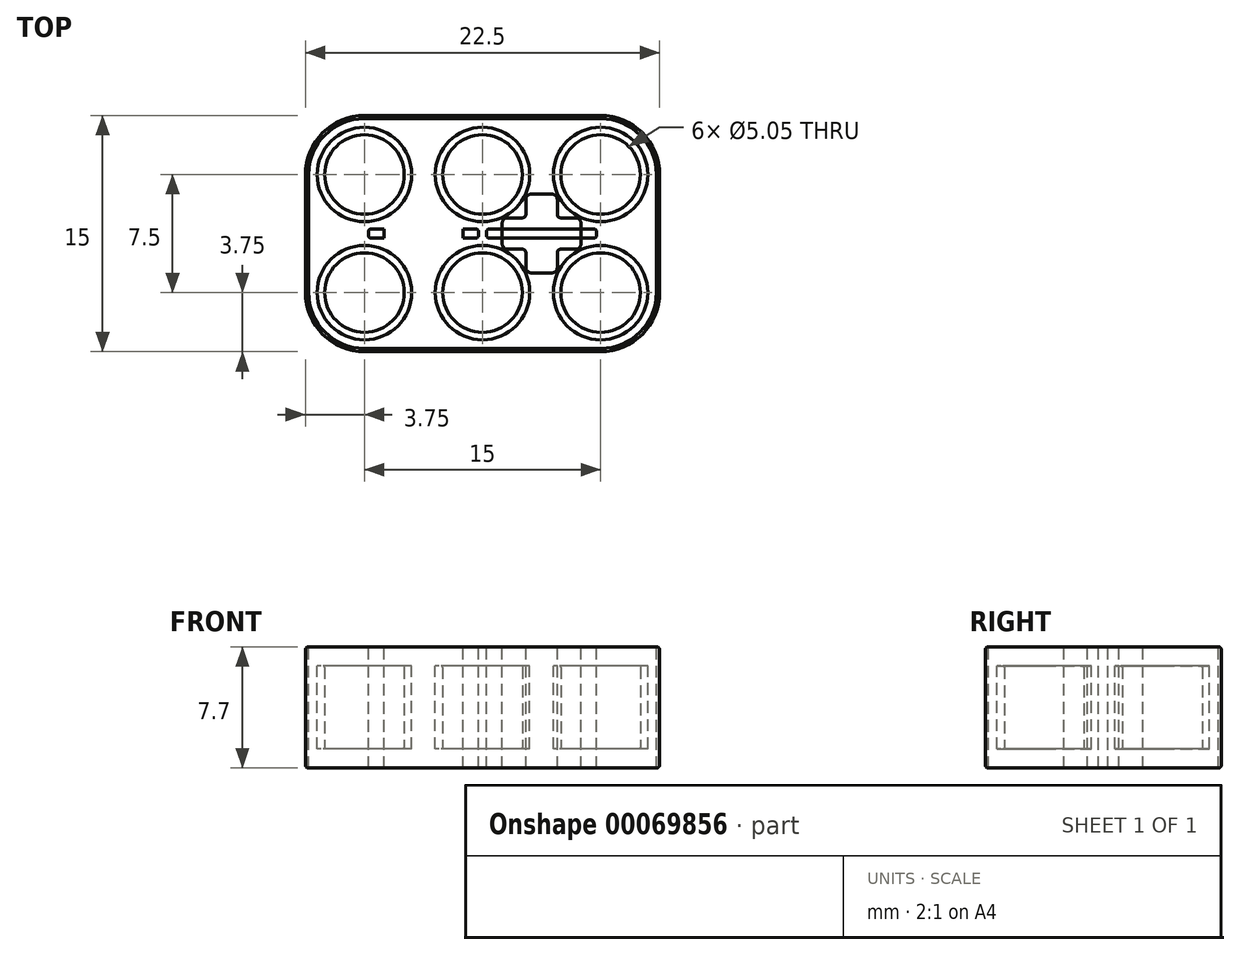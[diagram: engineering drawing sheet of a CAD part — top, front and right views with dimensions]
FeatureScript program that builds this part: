
annotation { "Feature Type Name" : "Feature", "Feature Type Description" : "" }
export const myFeature = defineFeature(function(context is Context, id is Id, definition is map)
    precondition{}
    {
        {
            var Q0;
            Q0=qCreatedBy(makeId("Top.planeOp"),FACE);
            var sketch = newSketch(context, id + "F0", { "sketchPlane" : qUnion([Q0])});
            skLineSegment(sketch, "E0.rect.bottom", {"start": v(7.5, -7.5) * mm, "end": v(-7.5, -7.5) * mm});
            skLineSegment(sketch, "E0.rect.top", {"start": v(7.5, 7.5) * mm, "end": v(-7.5, 7.5) * mm});
            skLineSegment(sketch, "E0.rect.left", {"start": v(11.25, -3.75) * mm, "end": v(11.25, 3.75) * mm});
            skLineSegment(sketch, "E0.rect.right", {"start": v(-11.25, -3.75) * mm, "end": v(-11.25, 3.75) * mm});
            skPoint(sketch, "E0.rect.middle", {"position": v(0, 0) * mm});
            skPoint(sketch, "E1.visualSharp", {"position": v(11.25, 7.5) * mm});
            skArc(sketch, "E1.filletArc", {"start": v(11.25, 3.75) * mm, "mid": v(10.15, 6.4) * mm, "end": v(7.5, 7.5) * mm});
            skPoint(sketch, "E2.visualSharp", {"position": v(-11.25, 7.5) * mm});
            skArc(sketch, "E2.filletArc", {"start": v(-7.5, 7.5) * mm, "mid": v(-10.15, 6.4) * mm, "end": v(-11.25, 3.75) * mm});
            skPoint(sketch, "E3.visualSharp", {"position": v(-11.25, -7.5) * mm});
            skArc(sketch, "E3.filletArc", {"start": v(-11.25, -3.75) * mm, "mid": v(-10.15, -6.4) * mm, "end": v(-7.5, -7.5) * mm});
            skPoint(sketch, "E4.visualSharp", {"position": v(11.25, -7.5) * mm});
            skArc(sketch, "E4.filletArc", {"start": v(7.5, -7.5) * mm, "mid": v(10.15, -6.4) * mm, "end": v(11.25, -3.75) * mm});
            skCircle(sketch, "E5", {"center": v(-7.5, 3.75) * mm, "radius": 2.52 * mm});
            skLineSegment(sketch, "E6", {"start": v(0, 0) * mm, "end": v(0, 7.5) * mm, "construction": true});
            skLineSegment(sketch, "E7", {"start": v(0, 0) * mm, "end": v(11.25, 0) * mm, "construction": true});
            skCircle(sketch, "E8.MirrorC", {"center": v(7.5, 3.75) * mm, "radius": 2.52 * mm});
            skCircle(sketch, "E9.MirrorC", {"center": v(7.5, -3.75) * mm, "radius": 2.52 * mm});
            skCircle(sketch, "E10.MirrorC", {"center": v(-7.5, -3.75) * mm, "radius": 2.52 * mm});
            skCircle(sketch, "E11", {"center": v(0, 3.75) * mm, "radius": 2.52 * mm});
            skCircle(sketch, "E12.MirrorC", {"center": v(0, -3.75) * mm, "radius": 2.52 * mm});
            skSolve(sketch);
        }
        {
            var Q0;
            Q0=qSketchRegion(id+"F0",true);
            extrude(context, id + "F1", {"entities" : qUnion([Q0]), "depth" : 3.85 * mm});
        }
        {
            var Q0;
            Q0=makeQuery(id+"F1.opExtrude","CAP_FACE",FACE,{"disambiguationData":[OSD([sQuery(id+"F0.wireOp",EDGE,"E0.rect.bottom"),sQuery(id+"F0.wireOp",EDGE,"E0.rect.top"),sQuery(id+"F0.wireOp",EDGE,"E0.rect.left"),sQuery(id+"F0.wireOp",EDGE,"E0.rect.right"),sQuery(id+"F0.wireOp",EDGE,"E1.filletArc"),sQuery(id+"F0.wireOp",EDGE,"E2.filletArc"),sQuery(id+"F0.wireOp",EDGE,"E3.filletArc"),sQuery(id+"F0.wireOp",EDGE,"E4.filletArc"),sQuery(id+"F0.wireOp",EDGE,"E5"),sQuery(id+"F0.wireOp",EDGE,"E8.MirrorC"),sQuery(id+"F0.wireOp",EDGE,"E9.MirrorC"),sQuery(id+"F0.wireOp",EDGE,"E10.MirrorC")])],"isStart":false});
            fillet(context, id + "F2", {"entities" : qUnion([Q0]), "radius" : 0.2 * mm, "tangentPropagation" : true, "allowEdgeOverflow" : false});
        }
        {
            var Q0;
            Q0=makeQuery(id+"F1.opExtrude","CAP_FACE",FACE,{"disambiguationData":[OSD([sQuery(id+"F0.wireOp",EDGE,"E0.rect.bottom"),sQuery(id+"F0.wireOp",EDGE,"E0.rect.top"),sQuery(id+"F0.wireOp",EDGE,"E0.rect.left"),sQuery(id+"F0.wireOp",EDGE,"E0.rect.right"),sQuery(id+"F0.wireOp",EDGE,"E1.filletArc"),sQuery(id+"F0.wireOp",EDGE,"E2.filletArc"),sQuery(id+"F0.wireOp",EDGE,"E3.filletArc"),sQuery(id+"F0.wireOp",EDGE,"E4.filletArc"),sQuery(id+"F0.wireOp",EDGE,"E5"),sQuery(id+"F0.wireOp",EDGE,"E8.MirrorC"),sQuery(id+"F0.wireOp",EDGE,"E9.MirrorC"),sQuery(id+"F0.wireOp",EDGE,"E10.MirrorC")])],"isStart":false});
            var sketch = newSketch(context, id + "F3", { "sketchPlane" : qUnion([Q0])});
            skCircle(sketch, "E13", {"center": v(-7.5, 3.75) * mm, "radius": 3 * mm});
            skCircle(sketch, "E14.MirrorC", {"center": v(7.5, 3.75) * mm, "radius": 3 * mm});
            skCircle(sketch, "E15.MirrorC", {"center": v(7.5, -3.75) * mm, "radius": 3 * mm});
            skCircle(sketch, "E16.MirrorC", {"center": v(-7.5, -3.75) * mm, "radius": 3 * mm});
            skCircle(sketch, "E17", {"center": v(0, 3.75) * mm, "radius": 3 * mm});
            skCircle(sketch, "E18.MirrorC", {"center": v(0, -3.75) * mm, "radius": 3 * mm});
            skSolve(sketch);
        }
        {
            var Q0;
            Q0=qSketchRegion(id+"F3",true);
            extrude(context, id + "F4", {"entities" : qUnion([Q0]), "operationType" : NewBodyOperationType.REMOVE, "oppositeDirection" : true, "depth" : 1.2 * mm});
        }
        {
            var Q0;
            Q0=makeQuery(id+"F4.boolean.opBoolean","COPY",EDGE,{"derivedFrom":makeQuery(id+"F4.opExtrude","CAP_EDGE",EDGE,{"disambiguationData":[OSD([sQuery(id+"F3.wireOp",EDGE,"E16.MirrorC")])],"isStart":true})});
            var Q1;
            Q1=makeQuery(id+"F4.boolean.opBoolean","INTERSECT",EDGE,{"derivedFrom":[makeQuery(id+"F1.opExtrude","SWEPT_FACE",FACE,{"disambiguationData":[OSD([sQuery(id+"F0.wireOp",EDGE,"E10.MirrorC")])]}),makeQuery(id+"F4.opExtrude","CAP_FACE",FACE,{"disambiguationData":[OSD([sQuery(id+"F3.wireOp",EDGE,"E16.MirrorC")])],"isStart":false})]});
            var Q2;
            Q2=makeQuery(id+"F4.boolean.opBoolean","COPY",EDGE,{"derivedFrom":makeQuery(id+"F4.opExtrude","CAP_EDGE",EDGE,{"disambiguationData":[OSD([sQuery(id+"F3.wireOp",EDGE,"E13")])],"isStart":true})});
            var Q3;
            Q3=makeQuery(id+"F4.boolean.opBoolean","INTERSECT",EDGE,{"derivedFrom":[makeQuery(id+"F1.opExtrude","SWEPT_FACE",FACE,{"disambiguationData":[OSD([sQuery(id+"F0.wireOp",EDGE,"E5")])]}),makeQuery(id+"F4.opExtrude","CAP_FACE",FACE,{"disambiguationData":[OSD([sQuery(id+"F3.wireOp",EDGE,"E13")])],"isStart":false})]});
            var Q4;
            Q4=makeQuery(id+"F4.boolean.opBoolean","COPY",EDGE,{"derivedFrom":makeQuery(id+"F4.opExtrude","CAP_EDGE",EDGE,{"disambiguationData":[OSD([sQuery(id+"F3.wireOp",EDGE,"E14.MirrorC")])],"isStart":true})});
            var Q5;
            Q5=makeQuery(id+"F4.boolean.opBoolean","INTERSECT",EDGE,{"derivedFrom":[makeQuery(id+"F1.opExtrude","SWEPT_FACE",FACE,{"disambiguationData":[OSD([sQuery(id+"F0.wireOp",EDGE,"E8.MirrorC")])]}),makeQuery(id+"F4.opExtrude","CAP_FACE",FACE,{"disambiguationData":[OSD([sQuery(id+"F3.wireOp",EDGE,"E14.MirrorC")])],"isStart":false})]});
            var Q6;
            Q6=makeQuery(id+"F4.boolean.opBoolean","INTERSECT",EDGE,{"derivedFrom":[makeQuery(id+"F1.opExtrude","SWEPT_FACE",FACE,{"disambiguationData":[OSD([sQuery(id+"F0.wireOp",EDGE,"E9.MirrorC")])]}),makeQuery(id+"F4.opExtrude","CAP_FACE",FACE,{"disambiguationData":[OSD([sQuery(id+"F3.wireOp",EDGE,"E15.MirrorC")])],"isStart":false})]});
            var Q7;
            Q7=makeQuery(id+"F4.boolean.opBoolean","COPY",EDGE,{"derivedFrom":makeQuery(id+"F4.opExtrude","CAP_EDGE",EDGE,{"disambiguationData":[OSD([sQuery(id+"F3.wireOp",EDGE,"E15.MirrorC")])],"isStart":true})});
            var Q8;
            Q8=makeQuery(id+"F4.boolean.opBoolean","COPY",EDGE,{"derivedFrom":makeQuery(id+"F4.opExtrude","CAP_EDGE",EDGE,{"disambiguationData":[OSD([sQuery(id+"F3.wireOp",EDGE,"E17")])],"isStart":true})});
            var Q9;
            Q9=makeQuery(id+"F4.boolean.opBoolean","INTERSECT",EDGE,{"derivedFrom":[makeQuery(id+"F1.opExtrude","SWEPT_FACE",FACE,{"disambiguationData":[OSD([sQuery(id+"F0.wireOp",EDGE,"E11")])]}),makeQuery(id+"F4.opExtrude","CAP_FACE",FACE,{"disambiguationData":[OSD([sQuery(id+"F3.wireOp",EDGE,"E17")])],"isStart":false})]});
            var Q10;
            Q10=makeQuery(id+"F4.boolean.opBoolean","COPY",EDGE,{"derivedFrom":makeQuery(id+"F4.opExtrude","CAP_EDGE",EDGE,{"disambiguationData":[OSD([sQuery(id+"F3.wireOp",EDGE,"E18.MirrorC")])],"isStart":true})});
            var Q11;
            Q11=makeQuery(id+"F4.boolean.opBoolean","INTERSECT",EDGE,{"derivedFrom":[makeQuery(id+"F1.opExtrude","SWEPT_FACE",FACE,{"disambiguationData":[OSD([sQuery(id+"F0.wireOp",EDGE,"E12.MirrorC")])]}),makeQuery(id+"F4.opExtrude","CAP_FACE",FACE,{"disambiguationData":[OSD([sQuery(id+"F3.wireOp",EDGE,"E18.MirrorC")])],"isStart":false})]});
            fillet(context, id + "F5", {"entities" : qUnion([Q0, Q1, Q2, Q3, Q4, Q5, Q6, Q7, Q8, Q9, Q10, Q11]), "radius" : 0.1 * mm, "tangentPropagation" : true, "allowEdgeOverflow" : false});
        }
        {
            var Q0;
            Q0=makeQuery(id+"F1.opExtrude","CAP_FACE",FACE,{"disambiguationData":[OSD([sQuery(id+"F0.wireOp",EDGE,"E0.rect.bottom"),sQuery(id+"F0.wireOp",EDGE,"E0.rect.top"),sQuery(id+"F0.wireOp",EDGE,"E0.rect.left"),sQuery(id+"F0.wireOp",EDGE,"E0.rect.right"),sQuery(id+"F0.wireOp",EDGE,"E1.filletArc"),sQuery(id+"F0.wireOp",EDGE,"E2.filletArc"),sQuery(id+"F0.wireOp",EDGE,"E3.filletArc"),sQuery(id+"F0.wireOp",EDGE,"E4.filletArc"),sQuery(id+"F0.wireOp",EDGE,"E5"),sQuery(id+"F0.wireOp",EDGE,"E8.MirrorC"),sQuery(id+"F0.wireOp",EDGE,"E9.MirrorC"),sQuery(id+"F0.wireOp",EDGE,"E10.MirrorC")])],"isStart":false});
            var sketch = newSketch(context, id + "F6", { "sketchPlane" : qUnion([Q0])});
            skPoint(sketch, "E19", {"position": v(-3.75, 0) * mm});
            skPoint(sketch, "E20.visualSharp", {"position": v(-7.25, 0.3) * mm});
            skPoint(sketch, "E21.visualSharp", {"position": v(-7.25, -0.3) * mm});
            skPoint(sketch, "E22.visualSharp", {"position": v(-4.75, -2.5) * mm});
            skPoint(sketch, "E23.visualSharp", {"position": v(-1.25, 1) * mm});
            skLineSegment(sketch, "E24.trimOffspring", {"start": v(-4.95, 1) * mm, "end": v(-5.9, 1) * mm});
            skLineSegment(sketch, "E25.trimOffspring", {"start": v(-2.75, -1.2) * mm, "end": v(-2.75, -2.15) * mm});
            skPoint(sketch, "E26.visualSharp", {"position": v(-2.75, 2.5) * mm});
            skPoint(sketch, "E27.visualSharp", {"position": v(-2.75, -2.5) * mm});
            skPoint(sketch, "E28.visualSharp", {"position": v(-6.25, 1) * mm});
            skLineSegment(sketch, "E29.rect.bottom", {"start": v(-3.1, 2.5) * mm, "end": v(-4.4, 2.5) * mm});
            skPoint(sketch, "E30.visualSharp", {"position": v(-6.25, -1) * mm});
            skPoint(sketch, "E31.visualSharp", {"position": v(-4.75, -1) * mm});
            skPoint(sketch, "E32.visualSharp", {"position": v(-1.25, -1) * mm});
            skPoint(sketch, "E33", {"position": v(-2.75, -1) * mm});
            skPoint(sketch, "E34", {"position": v(-4.75, 1) * mm});
            skPoint(sketch, "E35.visualSharp", {"position": v(-4.75, 2.5) * mm});
            skLineSegment(sketch, "E36.rect.top", {"start": v(-0.45, 0.3) * mm, "end": v(-7.05, 0.3) * mm});
            skLineSegment(sketch, "E37.rect.bottom", {"start": v(-1.6, -1) * mm, "end": v(-2.55, -1) * mm});
            skLineSegment(sketch, "E37.rect.top", {"start": v(-1.6, 1) * mm, "end": v(-2.55, 1) * mm});
            skLineSegment(sketch, "E37.rect.left", {"start": v(-1.25, -0.65) * mm, "end": v(-1.25, 0.65) * mm});
            skLineSegment(sketch, "E38.trimOffspring", {"start": v(-4.75, -1.2) * mm, "end": v(-4.75, -2.15) * mm});
            skLineSegment(sketch, "E37.rect.right", {"start": v(-6.25, -0.65) * mm, "end": v(-6.25, 0.65) * mm});
            skLineSegment(sketch, "E29.rect.top", {"start": v(-3.1, -2.5) * mm, "end": v(-4.4, -2.5) * mm});
            skLineSegment(sketch, "E36.rect.bottom", {"start": v(-0.45, -0.3) * mm, "end": v(-7.05, -0.3) * mm});
            skPoint(sketch, "E39", {"position": v(-2.75, 1) * mm});
            skLineSegment(sketch, "E29.rect.right", {"start": v(-4.75, 2.15) * mm, "end": v(-4.75, 1.2) * mm});
            skLineSegment(sketch, "E40.trimOffspring", {"start": v(-4.95, -1) * mm, "end": v(-5.9, -1) * mm});
            skLineSegment(sketch, "E29.rect.left", {"start": v(-2.75, 2.15) * mm, "end": v(-2.75, 1.2) * mm});
            skArc(sketch, "E31.filletArc", {"start": v(-4.75, -1.2) * mm, "mid": v(-4.8, -1.06) * mm, "end": v(-4.95, -1) * mm});
            skArc(sketch, "E27.filletArc", {"start": v(-3.1, -2.5) * mm, "mid": v(-2.85, -2.4) * mm, "end": v(-2.75, -2.15) * mm});
            skArc(sketch, "E32.filletArc", {"start": v(-1.6, -1) * mm, "mid": v(-1.35, -0.9) * mm, "end": v(-1.25, -0.65) * mm});
            skArc(sketch, "E26.filletArc", {"start": v(-2.75, 2.15) * mm, "mid": v(-2.85, 2.4) * mm, "end": v(-3.1, 2.5) * mm});
            skArc(sketch, "E28.filletArc", {"start": v(-5.9, 1) * mm, "mid": v(-6.15, 0.9) * mm, "end": v(-6.25, 0.65) * mm});
            skArc(sketch, "E23.filletArc", {"start": v(-1.25, 0.65) * mm, "mid": v(-1.35, 0.9) * mm, "end": v(-1.6, 1) * mm});
            skArc(sketch, "E30.filletArc", {"start": v(-6.25, -0.65) * mm, "mid": v(-6.15, -0.9) * mm, "end": v(-5.9, -1) * mm});
            skArc(sketch, "E22.filletArc", {"start": v(-4.75, -2.15) * mm, "mid": v(-4.65, -2.4) * mm, "end": v(-4.4, -2.5) * mm});
            skArc(sketch, "E21.filletArc", {"start": v(-7.25, -0.1) * mm, "mid": v(-7.2, -0.24) * mm, "end": v(-7.05, -0.3) * mm});
            skLineSegment(sketch, "E36.rect.right", {"start": v(-7.25, -0.1) * mm, "end": v(-7.25, 0.1) * mm});
            skArc(sketch, "E41.filletArc", {"start": v(-0.45, -0.3) * mm, "mid": v(-0.3, -0.24) * mm, "end": v(-0.25, -0.1) * mm});
            skArc(sketch, "E42.filletArc", {"start": v(-0.25, 0.1) * mm, "mid": v(-0.3, 0.24) * mm, "end": v(-0.45, 0.3) * mm});
            skLineSegment(sketch, "E36.rect.left", {"start": v(-0.25, -0.1) * mm, "end": v(-0.25, 0.1) * mm});
            skArc(sketch, "E20.filletArc", {"start": v(-7.05, 0.3) * mm, "mid": v(-7.2, 0.24) * mm, "end": v(-7.25, 0.1) * mm});
            skArc(sketch, "E35.filletArc", {"start": v(-4.4, 2.5) * mm, "mid": v(-4.65, 2.4) * mm, "end": v(-4.75, 2.15) * mm});
            skArc(sketch, "E43.filletArc", {"start": v(-4.95, 1) * mm, "mid": v(-4.8, 1.06) * mm, "end": v(-4.75, 1.2) * mm});
            skArc(sketch, "E44.filletArc", {"start": v(-2.75, 1.2) * mm, "mid": v(-2.7, 1.06) * mm, "end": v(-2.55, 1) * mm});
            skArc(sketch, "E45.filletArc", {"start": v(-2.55, -1) * mm, "mid": v(-2.7, -1.06) * mm, "end": v(-2.75, -1.2) * mm});
            skArc(sketch, "E46.MirrorCS", {"start": v(4.95, 1) * mm, "mid": v(4.8, 1.06) * mm, "end": v(4.75, 1.2) * mm});
            skArc(sketch, "E47.MirrorCS", {"start": v(7.05, 0.3) * mm, "mid": v(7.2, 0.24) * mm, "end": v(7.25, 0.1) * mm});
            skLineSegment(sketch, "E48.MirrorCS", {"start": v(7.25, -0.1) * mm, "end": v(7.25, 0.1) * mm});
            skArc(sketch, "E49.MirrorCS", {"start": v(7.25, -0.1) * mm, "mid": v(7.2, -0.24) * mm, "end": v(7.05, -0.3) * mm});
            skPoint(sketch, "E50.MirrorP", {"position": v(3.75, 0) * mm});
            skArc(sketch, "E51.MirrorCS", {"start": v(4.4, 2.5) * mm, "mid": v(4.65, 2.4) * mm, "end": v(4.75, 2.15) * mm});
            skArc(sketch, "E52.MirrorCS", {"start": v(1.25, 0.65) * mm, "mid": v(1.35, 0.9) * mm, "end": v(1.6, 1) * mm});
            skArc(sketch, "E53.MirrorCS", {"start": v(0.45, -0.3) * mm, "mid": v(0.3, -0.24) * mm, "end": v(0.25, -0.1) * mm});
            skArc(sketch, "E54.MirrorCS", {"start": v(1.6, -1) * mm, "mid": v(1.35, -0.9) * mm, "end": v(1.25, -0.65) * mm});
            skArc(sketch, "E55.MirrorCS", {"start": v(2.55, -1) * mm, "mid": v(2.7, -1.06) * mm, "end": v(2.75, -1.2) * mm});
            skLineSegment(sketch, "E56.MirrorCS", {"start": v(0.25, -0.1) * mm, "end": v(0.25, 0.1) * mm});
            skArc(sketch, "E57.MirrorCS", {"start": v(0.25, 0.1) * mm, "mid": v(0.3, 0.24) * mm, "end": v(0.45, 0.3) * mm});
            skArc(sketch, "E58.MirrorCS", {"start": v(6.25, -0.65) * mm, "mid": v(6.15, -0.9) * mm, "end": v(5.9, -1) * mm});
            skArc(sketch, "E59.MirrorCS", {"start": v(2.75, 2.15) * mm, "mid": v(2.85, 2.4) * mm, "end": v(3.1, 2.5) * mm});
            skArc(sketch, "E60.MirrorCS", {"start": v(4.75, -2.15) * mm, "mid": v(4.65, -2.4) * mm, "end": v(4.4, -2.5) * mm});
            skArc(sketch, "E61.MirrorCS", {"start": v(2.75, 1.2) * mm, "mid": v(2.7, 1.06) * mm, "end": v(2.55, 1) * mm});
            skArc(sketch, "E62.MirrorCS", {"start": v(3.1, -2.5) * mm, "mid": v(2.85, -2.4) * mm, "end": v(2.75, -2.15) * mm});
            skArc(sketch, "E63.MirrorCS", {"start": v(4.75, -1.2) * mm, "mid": v(4.8, -1.06) * mm, "end": v(4.95, -1) * mm});
            skArc(sketch, "E64.MirrorCS", {"start": v(5.9, 1) * mm, "mid": v(6.15, 0.9) * mm, "end": v(6.25, 0.65) * mm});
            skPoint(sketch, "E65.MirrorP", {"position": v(2.75, 1) * mm});
            skPoint(sketch, "E66.MirrorP", {"position": v(4.75, 1) * mm});
            skPoint(sketch, "E67.MirrorP", {"position": v(2.75, -1) * mm});
            skPoint(sketch, "E68.MirrorP", {"position": v(4.75, -1) * mm});
            skLineSegment(sketch, "E69.MirrorCS", {"start": v(4.75, 2.15) * mm, "end": v(4.75, 1.2) * mm});
            skLineSegment(sketch, "E70.MirrorCS", {"start": v(1.6, 1) * mm, "end": v(2.55, 1) * mm});
            skPoint(sketch, "E71.MirrorP", {"position": v(1.25, 1) * mm});
            skPoint(sketch, "E72.MirrorP", {"position": v(6.25, 1) * mm});
            skPoint(sketch, "E73.MirrorP", {"position": v(7.25, 0.3) * mm});
            skLineSegment(sketch, "E74.MirrorCS", {"start": v(0.45, 0.3) * mm, "end": v(7.05, 0.3) * mm});
            skLineSegment(sketch, "E75.MirrorCS", {"start": v(0.45, -0.3) * mm, "end": v(7.05, -0.3) * mm});
            skLineSegment(sketch, "E76.MirrorCS", {"start": v(6.25, -0.65) * mm, "end": v(6.25, 0.65) * mm});
            skPoint(sketch, "E77.MirrorP", {"position": v(7.25, -0.3) * mm});
            skLineSegment(sketch, "E78.MirrorCS", {"start": v(1.6, -1) * mm, "end": v(2.55, -1) * mm});
            skLineSegment(sketch, "E79.MirrorCS", {"start": v(4.95, -1) * mm, "end": v(5.9, -1) * mm});
            skLineSegment(sketch, "E80.MirrorCS", {"start": v(4.75, -1.2) * mm, "end": v(4.75, -2.15) * mm});
            skLineSegment(sketch, "E81.MirrorCS", {"start": v(3.1, -2.5) * mm, "end": v(4.4, -2.5) * mm});
            skPoint(sketch, "E82.MirrorP", {"position": v(2.75, 2.5) * mm});
            skPoint(sketch, "E83.MirrorP", {"position": v(6.25, -1) * mm});
            skPoint(sketch, "E84.MirrorP", {"position": v(1.25, -1) * mm});
            skLineSegment(sketch, "E85.MirrorCS", {"start": v(3.1, 2.5) * mm, "end": v(4.4, 2.5) * mm});
            skLineSegment(sketch, "E86.MirrorCS", {"start": v(1.25, -0.65) * mm, "end": v(1.25, 0.65) * mm});
            skLineSegment(sketch, "E87.MirrorCS", {"start": v(4.95, 1) * mm, "end": v(5.9, 1) * mm});
            skLineSegment(sketch, "E88.MirrorCS", {"start": v(2.75, 2.15) * mm, "end": v(2.75, 1.2) * mm});
            skPoint(sketch, "E89.MirrorP", {"position": v(4.75, -2.5) * mm});
            skPoint(sketch, "E90.MirrorP", {"position": v(2.75, -2.5) * mm});
            skPoint(sketch, "E91.MirrorP", {"position": v(4.75, 2.5) * mm});
            skLineSegment(sketch, "E92.MirrorCS", {"start": v(2.75, -1.2) * mm, "end": v(2.75, -2.15) * mm});
            skSolve(sketch);
        }
        {
            var Q0;
            {var subQ1=sQuery(id+"F6.wireOp",EDGE,"E24.trimOffspring");Q0=makeQuery(id+"F6.imprint","IMPRINT",FACE,{"disambiguationData":[TD([[makeQuery(id+"F6.imprint","IMPRINT",EDGE,{"derivedFrom":subQ1}),1.0]])]});}
            var Q1;
            Q1=makeQuery(id+"F6.imprint","IMPRINT",FACE,{"disambiguationData":[TD([[makeQuery(id+"F6.imprint","IMPRINT",EDGE,{"derivedFrom":sQuery(id+"F6.wireOp",EDGE,"E25.trimOffspring")}),-1.0]])]});
            var Q2;
            Q2=makeQuery(id+"F6.imprint","IMPRINT",FACE,{"disambiguationData":[TD([[makeQuery(id+"F6.imprint","IMPRINT",EDGE,{"derivedFrom":sQuery(id+"F6.wireOp",EDGE,"0f8df71c-6bcd-472b-bdd1-81162fe7ee0e.trimOffspring")}),1.0]])]});
            var Q3;
            Q3=makeQuery(id+"F6.imprint","IMPRINT",FACE,{"disambiguationData":[TD([[makeQuery(id+"F6.imprint","IMPRINT",EDGE,{"derivedFrom":sQuery(id+"F6.wireOp",EDGE,"ae506f7c-1ef5-4ce8-9eb2-6ec652579db3.trimOffspring")}),-1.0]])]});
            var Q4;
            {var subQ0=sQuery(id+"F6.wireOp",EDGE,"467c052d-1678-41fc-b83b-6d79ee630ae4.rect.left");var subQ1=sQuery(id+"F6.wireOp",EDGE,"2fcfc1e4-8fe4-44b0-879c-1b8382a30255.rect.top");var subQ2=makeQuery(id+"F6.imprint","INTERSECT",VERTEX,{"derivedFrom":[subQ1,subQ0]});Q4=makeQuery(id+"F6.imprint","IMPRINT",FACE,{"disambiguationData":[TD([[makeQuery(id+"F6.imprint","IMPRINT",EDGE,{"disambiguationData":[TD([[subQ2,-1.0]])],"derivedFrom":subQ1}),1.0]])]});}
            var Q5;
            {var subQ0=sQuery(id+"F6.wireOp",EDGE,"E37.rect.left");var subQ1=sQuery(id+"F6.wireOp",EDGE,"E36.rect.top");var subQ2=makeQuery(id+"F6.imprint","INTERSECT",VERTEX,{"derivedFrom":[subQ1,subQ0]});Q5=makeQuery(id+"F6.imprint","IMPRINT",FACE,{"disambiguationData":[TD([[makeQuery(id+"F6.imprint","IMPRINT",EDGE,{"disambiguationData":[TD([[subQ2,-1.0]])],"derivedFrom":subQ1}),1.0]])]});}
            var Q6;
            {var subQ0=sQuery(id+"F6.wireOp",EDGE,"20d6213e-901f-4b86-adbe-36261a4a20df.filletArc");Q6=makeQuery(id+"F6.imprint","IMPRINT",FACE,{"disambiguationData":[TD([[makeQuery(id+"F6.imprint","IMPRINT",EDGE,{"derivedFrom":subQ0}),1.0]])]});}
            var Q7;
            {var subQ0=sQuery(id+"F6.wireOp",EDGE,"fe9a76bd-dc21-48b8-89e2-0647019f0883.filletArc");Q7=makeQuery(id+"F6.imprint","IMPRINT",FACE,{"disambiguationData":[TD([[makeQuery(id+"F6.imprint","IMPRINT",EDGE,{"derivedFrom":subQ0}),1.0]])]});}
            var Q8;
            Q8=makeQuery(id+"F6.imprint","IMPRINT",FACE,{"disambiguationData":[TD([[makeQuery(id+"F6.imprint","IMPRINT",EDGE,{"derivedFrom":sQuery(id+"F6.wireOp",EDGE,"E46.MirrorCS")}),1.0]])]});
            var Q9;
            {var subQ0=sQuery(id+"F6.wireOp",EDGE,"E86.MirrorCS");var subQ1=sQuery(id+"F6.wireOp",EDGE,"E74.MirrorCS");var subQ2=makeQuery(id+"F6.imprint","INTERSECT",VERTEX,{"derivedFrom":[subQ1,subQ0]});Q9=makeQuery(id+"F6.imprint","IMPRINT",FACE,{"disambiguationData":[TD([[makeQuery(id+"F6.imprint","IMPRINT",EDGE,{"disambiguationData":[TD([[subQ2,-1.0]])],"derivedFrom":subQ1}),-1.0]])]});}
            var Q10;
            Q10=makeQuery(id+"F6.imprint","IMPRINT",FACE,{"disambiguationData":[TD([[makeQuery(id+"F6.imprint","IMPRINT",EDGE,{"derivedFrom":sQuery(id+"F6.wireOp",EDGE,"E55.MirrorCS")}),1.0]])]});
            var Q11;
            Q11=qCreatedBy(makeId("Top.planeOp"),FACE);
            extrude(context, id + "F7", {"entities" : qUnion([Q0, Q1, Q2, Q3, Q4, Q5, Q6, Q7, Q8, Q9, Q10]), "operationType" : NewBodyOperationType.REMOVE, "endBound" : BoundingType.UP_TO_SURFACE, "oppositeDirection" : true, "endBoundEntityFace" : qUnion([Q11]), "depth" : 25 * mm});
        }
        {
            var Q0;
            Q0=makeQuery(id+"F1.opExtrude","SWEPT_BODY",BODY,{"disambiguationData":[OSD([sQuery(id+"F0.wireOp",EDGE,"E0.rect.bottom"),sQuery(id+"F0.wireOp",EDGE,"E0.rect.top"),sQuery(id+"F0.wireOp",EDGE,"E0.rect.left"),sQuery(id+"F0.wireOp",EDGE,"E0.rect.right"),sQuery(id+"F0.wireOp",EDGE,"E1.filletArc"),sQuery(id+"F0.wireOp",EDGE,"E2.filletArc"),sQuery(id+"F0.wireOp",EDGE,"E3.filletArc"),sQuery(id+"F0.wireOp",EDGE,"E4.filletArc"),sQuery(id+"F0.wireOp",EDGE,"E5"),sQuery(id+"F0.wireOp",EDGE,"E8.MirrorC"),sQuery(id+"F0.wireOp",EDGE,"E9.MirrorC"),sQuery(id+"F0.wireOp",EDGE,"E10.MirrorC")])]});
            var Q1;
            Q1=qCreatedBy(makeId("Top.planeOp"),FACE);
            mirror(context, id + "F8", {"operationType" : NewBodyOperationType.ADD, "entities" : qUnion([Q0]), "mirrorPlane" : qUnion([Q1])});
        }
    });
